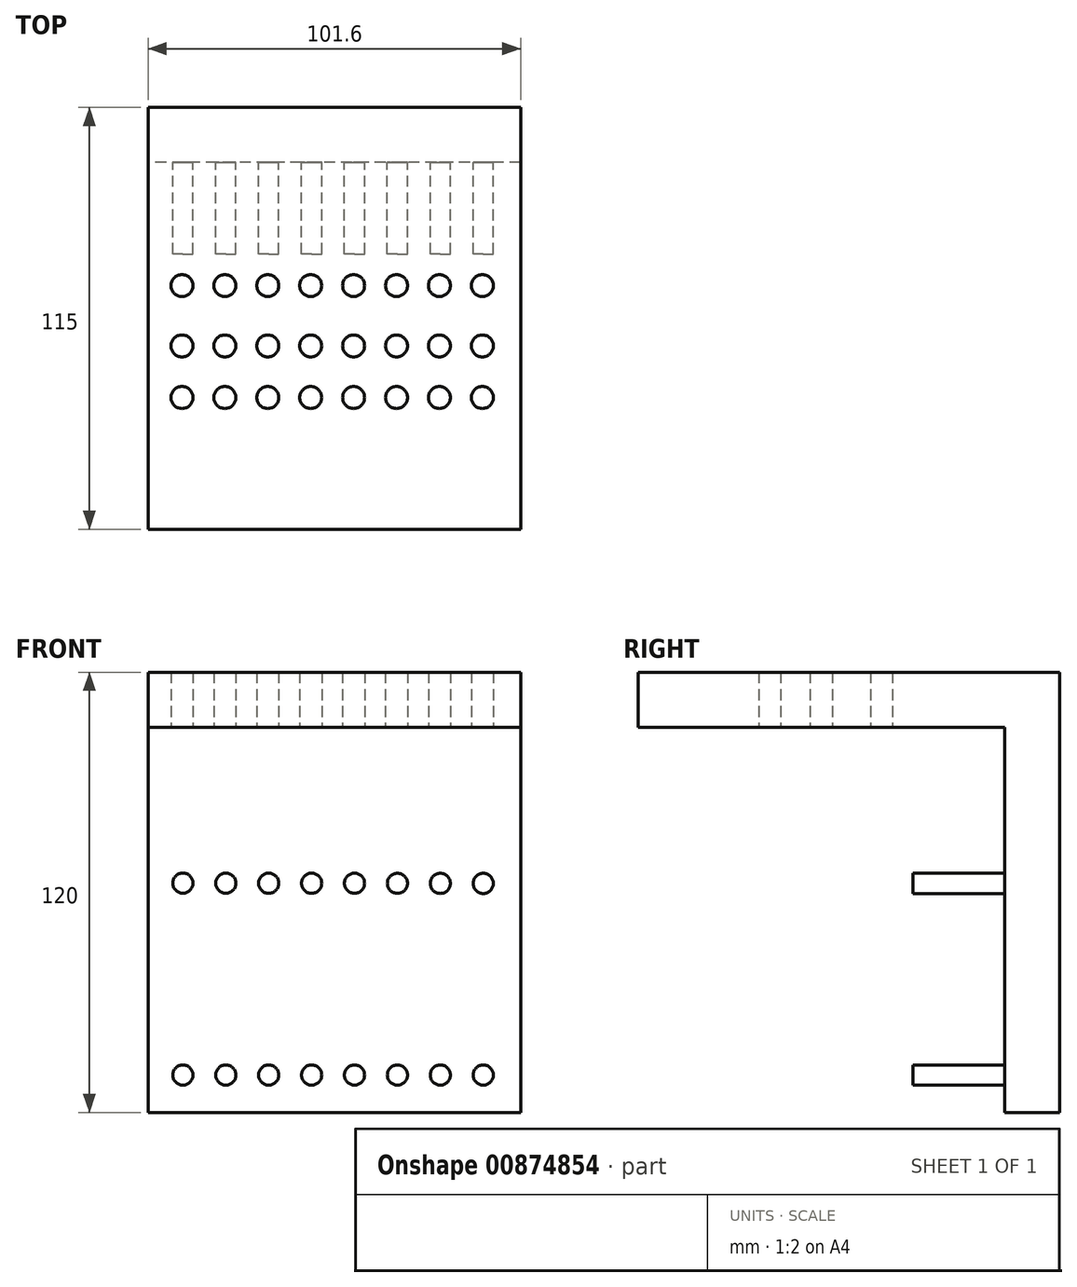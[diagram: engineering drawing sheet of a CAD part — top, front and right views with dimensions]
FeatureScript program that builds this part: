
annotation { "Feature Type Name" : "Feature", "Feature Type Description" : "" }
export const myFeature = defineFeature(function(context is Context, id is Id, definition is map)
    precondition{}
    {
        {
            var Q0;
            Q0=qCreatedBy(makeId("Right.planeOp"),FACE);
            var sketch = newSketch(context, id + "F0", { "sketchPlane" : qUnion([Q0])});
            skLineSegment(sketch, "E0", {"start": v(-134.57, 118.7) * mm, "end": v(-34.57, 118.7) * mm});
            skLineSegment(sketch, "E1", {"start": v(-34.57, 118.7) * mm, "end": v(-34.57, 13.7) * mm});
            skLineSegment(sketch, "E2", {"start": v(-34.57, 13.7) * mm, "end": v(-19.57, 13.7) * mm});
            skLineSegment(sketch, "E3", {"start": v(-19.57, 13.7) * mm, "end": v(-19.57, 133.7) * mm});
            skLineSegment(sketch, "E4", {"start": v(-19.57, 133.7) * mm, "end": v(-134.57, 133.7) * mm});
            skPoint(sketch, "E5.start.orphan", {"position": v(-134.57, 130.44) * mm});
            skLineSegment(sketch, "E6", {"start": v(-134.57, 118.7) * mm, "end": v(-134.57, 133.7) * mm});
            skSolve(sketch);
        }
        {
            var Q0;
            Q0 = qSketchRegion(id + "F0", true);
            extrude(context, id + "F1", {"entities" : qUnion([Q0]), "depth" : 101.6 * mm, "offsetDistance" : 25.4 * mm});
        }
        {
            var Q0;
            Q0=makeQuery(id+"F1.opExtrude","SWEPT_FACE",FACE,{"disambiguationData":[OSD([sQuery(id+"F0.wireOp",EDGE,"E1")])]});
            var sketch = newSketch(context, id + "F2", { "sketchPlane" : qUnion([Q0])});
            skCircle(sketch, "E7", {"center": v(9.5, 23.9) * mm, "radius": 2.75 * mm});
            skCircle(sketch, "E8.1.0.0", {"center": v(21.2, 23.9) * mm, "radius": 2.75 * mm});
            skCircle(sketch, "E8.2.0.0", {"center": v(32.9, 23.9) * mm, "radius": 2.75 * mm});
            skCircle(sketch, "E8.3.0.0", {"center": v(44.6, 23.9) * mm, "radius": 2.75 * mm});
            skCircle(sketch, "E8.4.0.0", {"center": v(56.3, 23.9) * mm, "radius": 2.75 * mm});
            skCircle(sketch, "E8.5.0.0", {"center": v(68, 23.9) * mm, "radius": 2.75 * mm});
            skCircle(sketch, "E8.6.0.0", {"center": v(79.7, 23.9) * mm, "radius": 2.75 * mm});
            skCircle(sketch, "E8.7.0.0", {"center": v(91.4, 23.9) * mm, "radius": 2.75 * mm});
            skLineSegment(sketch, "E8.direction1", {"start": v(9.5, 23.9) * mm, "end": v(21.2, 23.9) * mm, "construction": true});
            skCircle(sketch, "E9", {"center": v(9.5, 76.21) * mm, "radius": 2.75 * mm});
            skCircle(sketch, "E10.1.0.0", {"center": v(21.2, 76.2) * mm, "radius": 2.75 * mm});
            skCircle(sketch, "E10.2.0.0", {"center": v(32.9, 76.19) * mm, "radius": 2.75 * mm});
            skCircle(sketch, "E10.3.0.0", {"center": v(44.6, 76.18) * mm, "radius": 2.75 * mm});
            skCircle(sketch, "E10.4.0.0", {"center": v(56.3, 76.17) * mm, "radius": 2.75 * mm});
            skCircle(sketch, "E10.5.0.0", {"center": v(68, 76.16) * mm, "radius": 2.75 * mm});
            skCircle(sketch, "E10.6.0.0", {"center": v(79.7, 76.14) * mm, "radius": 2.75 * mm});
            skCircle(sketch, "E10.7.0.0", {"center": v(91.4, 76.13) * mm, "radius": 2.75 * mm});
            skLineSegment(sketch, "E10.direction1", {"start": v(9.5, 76.21) * mm, "end": v(21.2, 76.2) * mm, "construction": true});
            skSolve(sketch);
        }
        {
            var Q0;
            Q0 = qSketchRegion(id + "F2", true);
            extrude(context, id + "F3", {"entities" : qUnion([Q0]), "operationType" : NewBodyOperationType.ADD, "depth" : 25 * mm, "offsetDistance" : 25 * mm});
        }
        {
            var Q0;
            Q0=makeQuery(id+"F1.opExtrude","SWEPT_FACE",FACE,{"disambiguationData":[OSD([sQuery(id+"F0.wireOp",EDGE,"E0")])]});
            var sketch = newSketch(context, id + "F4", { "sketchPlane" : qUnion([Q0])});
            skCircle(sketch, "E11", {"center": v(9.25, 68.16) * mm, "radius": 3 * mm});
            skCircle(sketch, "E12.1.0.0", {"center": v(20.95, 68.16) * mm, "radius": 3 * mm});
            skCircle(sketch, "E12.2.0.0", {"center": v(32.65, 68.16) * mm, "radius": 3 * mm});
            skCircle(sketch, "E12.3.0.0", {"center": v(44.35, 68.16) * mm, "radius": 3 * mm});
            skCircle(sketch, "E12.4.0.0", {"center": v(56.05, 68.16) * mm, "radius": 3 * mm});
            skCircle(sketch, "E12.5.0.0", {"center": v(67.75, 68.16) * mm, "radius": 3 * mm});
            skCircle(sketch, "E12.6.0.0", {"center": v(79.45, 68.16) * mm, "radius": 3 * mm});
            skCircle(sketch, "E12.7.0.0", {"center": v(91.15, 68.16) * mm, "radius": 3 * mm});
            skLineSegment(sketch, "E12.direction1", {"start": v(9.25, 68.16) * mm, "end": v(20.95, 68.16) * mm, "construction": true});
            skCircle(sketch, "E13", {"center": v(9.25, 84.6) * mm, "radius": 3 * mm});
            skCircle(sketch, "E14.1.0.0", {"center": v(20.95, 84.6) * mm, "radius": 3 * mm});
            skCircle(sketch, "E14.2.0.0", {"center": v(32.65, 84.6) * mm, "radius": 3 * mm});
            skCircle(sketch, "E14.3.0.0", {"center": v(44.35, 84.6) * mm, "radius": 3 * mm});
            skCircle(sketch, "E14.4.0.0", {"center": v(56.05, 84.6) * mm, "radius": 3 * mm});
            skCircle(sketch, "E14.5.0.0", {"center": v(67.75, 84.6) * mm, "radius": 3 * mm});
            skCircle(sketch, "E14.6.0.0", {"center": v(79.45, 84.6) * mm, "radius": 3 * mm});
            skCircle(sketch, "E14.7.0.0", {"center": v(91.15, 84.6) * mm, "radius": 3 * mm});
            skLineSegment(sketch, "E14.direction1", {"start": v(9.25, 84.6) * mm, "end": v(20.95, 84.6) * mm, "construction": true});
            skCircle(sketch, "E15", {"center": v(9.25, 98.67) * mm, "radius": 3 * mm});
            skCircle(sketch, "E16.1.0.0", {"center": v(20.95, 98.67) * mm, "radius": 3 * mm});
            skCircle(sketch, "E16.2.0.0", {"center": v(32.65, 98.67) * mm, "radius": 3 * mm});
            skCircle(sketch, "E16.3.0.0", {"center": v(44.35, 98.67) * mm, "radius": 3 * mm});
            skCircle(sketch, "E16.4.0.0", {"center": v(56.05, 98.67) * mm, "radius": 3 * mm});
            skCircle(sketch, "E16.5.0.0", {"center": v(67.75, 98.67) * mm, "radius": 3 * mm});
            skCircle(sketch, "E16.6.0.0", {"center": v(79.45, 98.67) * mm, "radius": 3 * mm});
            skCircle(sketch, "E16.7.0.0", {"center": v(91.15, 98.67) * mm, "radius": 3 * mm});
            skLineSegment(sketch, "E16.direction1", {"start": v(9.25, 98.67) * mm, "end": v(20.95, 98.67) * mm, "construction": true});
            skSolve(sketch);
        }
        {
            var Q0;
            Q0 = qSketchRegion(id + "F4", true);
            extrude(context, id + "F5", {"entities" : qUnion([Q0]), "operationType" : NewBodyOperationType.REMOVE, "oppositeDirection" : true, "depth" : 30 * mm, "offsetDistance" : 25 * mm});
        }
    });
